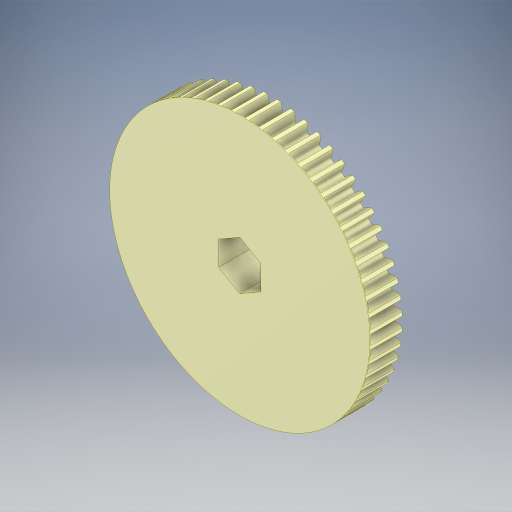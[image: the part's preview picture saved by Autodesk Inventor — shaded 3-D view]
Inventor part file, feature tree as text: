
AUTODESK INVENTOR PART (.ipt)
format: ipt  version: 2024 (Build 280153000, 153)  size: 1,947,648 bytes
history: native  units: in
note: dims shown in document units (in); Inventor stores cm internally (conversion verified against a paired STEP export)
features: extrude x3, sketch x3, projected_geometry x1, boolean_combine x1
ambient origin geometry x8: Origin, YZ Plane, XZ Plane, XY Plane, X Axis, Y Axis, Z Axis, Center Point
bodies: Solid1 (feature_tree)
feature tree (8):
  extrude  "Extrusion1"  Depth=1.0in TaperAngle=0.0deg
  extrude  "Extrusion2"  [1 undecoded]
  extrude  "Extrusion3"  [1 undecoded]
  sketch  "Sketch1"  dims[d0=1.0in d1=0.0in d2=1.0in d3=0.0in]
  sketch  "Sketch2"  dims[d4=0.01in d5=0.0in]
  sketch  "Sketch3"
  projected_geometry  "Projected Loop1"
  boolean_combine  "Combine1"
note: 2 required parameter values undecoded (feature->parameter linkage not recoverable at this tier; creation-order binding heuristic only, values carry confidence <= 0.55)
